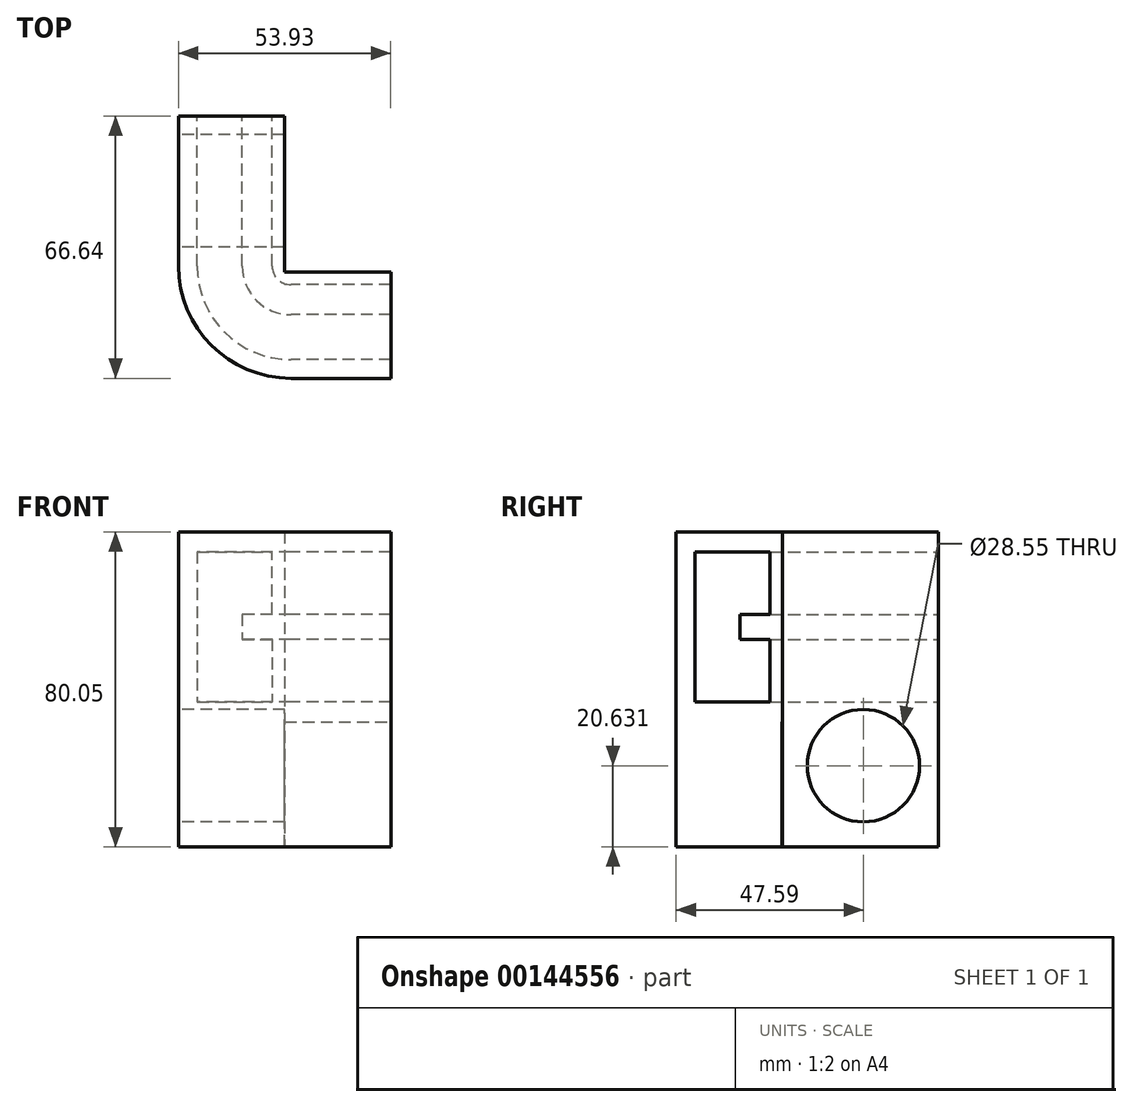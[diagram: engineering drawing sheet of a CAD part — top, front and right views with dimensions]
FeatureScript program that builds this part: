
annotation { "Feature Type Name" : "Feature", "Feature Type Description" : "" }
export const myFeature = defineFeature(function(context is Context, id is Id, definition is map)
    precondition{}
    {
        {
            var Q0;
            Q0=qCreatedBy(makeId("Front.planeOp"),FACE);
            var sketch = newSketch(context, id + "F0", { "sketchPlane" : qUnion([Q0])});
            skLineSegment(sketch, "E0.bottom", {"start": v(-12.7, 18.7) * mm, "end": v(6.35, 18.7) * mm});
            skLineSegment(sketch, "E0.top", {"start": v(-12.7, -19.4) * mm, "end": v(6.35, -19.4) * mm});
            skLineSegment(sketch, "E0.left", {"start": v(-12.7, 18.7) * mm, "end": v(-12.7, -19.4) * mm});
            skLineSegment(sketch, "E1", {"start": v(6.35, -3.53) * mm, "end": v(6.35, -19.4) * mm});
            skLineSegment(sketch, "E2", {"start": v(6.35, 2.82) * mm, "end": v(6.35, 18.7) * mm});
            skLineSegment(sketch, "E3", {"start": v(6.35, 2.82) * mm, "end": v(-1.27, 2.82) * mm});
            skLineSegment(sketch, "E4.bottom", {"start": v(-1.27, 2.82) * mm, "end": v(6.35, 2.82) * mm});
            skLineSegment(sketch, "E4.top", {"start": v(-1.27, -3.53) * mm, "end": v(6.35, -3.53) * mm});
            skLineSegment(sketch, "E4.left", {"start": v(-1.27, 2.82) * mm, "end": v(-1.27, -3.53) * mm});
            skLineSegment(sketch, "E5.bottom", {"start": v(-17.44, 23.8) * mm, "end": v(11.1, 23.8) * mm});
            skLineSegment(sketch, "E5.top", {"start": v(-17.44, -24.5) * mm, "end": v(11.1, -24.5) * mm});
            skLineSegment(sketch, "E5.left", {"start": v(-17.44, 23.8) * mm, "end": v(-17.44, -24.5) * mm});
            skLineSegment(sketch, "E5.right", {"start": v(11.1, 23.8) * mm, "end": v(11.1, -24.5) * mm});
            skLineSegment(sketch, "E6", {"start": v(-12.7, 18.7) * mm, "end": v(-17.44, 23.8) * mm, "construction": true});
            skLineSegment(sketch, "E7", {"start": v(6.35, 18.7) * mm, "end": v(11.1, 23.8) * mm, "construction": true});
            skLineSegment(sketch, "E8", {"start": v(6.35, -19.4) * mm, "end": v(11.1, -24.5) * mm, "construction": true});
            skLineSegment(sketch, "E9", {"start": v(-17.44, -24.5) * mm, "end": v(-12.7, -19.4) * mm, "construction": true});
            skSolve(sketch);
        }
        {
            var Q0;
            Q0=makeQuery(id+"F0.imprint","IMPRINT",FACE,{"disambiguationData":[TD([[makeQuery(id+"F0.imprint","IMPRINT",EDGE,{"derivedFrom":sQuery(id+"F0.wireOp",EDGE,"E0.bottom")}),1.0]])]});
            var Q1;
            Q1=sQuery(id+"F0.wireOp",EDGE,"E8");
            var Q2;
            Q2=sQuery(id+"F0.wireOp",EDGE,"E9");
            var Q3;
            Q3=sQuery(id+"F0.wireOp",EDGE,"E6");
            var Q4;
            Q4=sQuery(id+"F0.wireOp",EDGE,"E7");
            extrude(context, id + "F1", {"entities" : qUnion([Q0]), "surfaceEntities" : qUnion([Q1, Q2, Q3, Q4]), "depth" : 25.4 * mm});
        }
        {
            var Q0;
            Q0=makeQuery(id+"F1.opExtrude","CAP_FACE",FACE,{"disambiguationData":[OSD([sQuery(id+"F0.wireOp",EDGE,"E0.bottom"),sQuery(id+"F0.wireOp",EDGE,"E0.top"),sQuery(id+"F0.wireOp",EDGE,"E0.left"),sQuery(id+"F0.wireOp",EDGE,"E1"),sQuery(id+"F0.wireOp",EDGE,"E2"),sQuery(id+"F0.wireOp",EDGE,"E4.bottom"),sQuery(id+"F0.wireOp",EDGE,"E4.top"),sQuery(id+"F0.wireOp",EDGE,"E4.left"),sQuery(id+"F0.wireOp",EDGE,"E5.bottom"),sQuery(id+"F0.wireOp",EDGE,"E5.top"),sQuery(id+"F0.wireOp",EDGE,"E5.left"),sQuery(id+"F0.wireOp",EDGE,"E5.right")])],"isStart":false});
            var Q1;
            Q1=makeQuery(id+"F1.opExtrude","CAP_EDGE",EDGE,{"disambiguationData":[OSD([sQuery(id+"F0.wireOp",EDGE,"E5.right")])],"isStart":false});
            revolve(context, id + "F2", {"operationType" : NewBodyOperationType.ADD, "entities" : qUnion([Q0]), "axis" : qUnion([Q1]), "revolveType" : RevolveType.ONE_DIRECTION, "oppositeDirection" : true, "angle" : 90 * degree});
        }
        {
            var Q0;
            {var subQ0=sQuery(id+"F0.wireOp",EDGE,"E5.right");Q0=makeQuery(id+"F2.boolean.opBoolean","MERGE",FACE,{"derivedFrom":[makeQuery(id+"F1.opExtrude","SWEPT_FACE",FACE,{"disambiguationData":[OSD([subQ0])]}),makeQuery(id+"F2.opRevolve","CAP_FACE",FACE,{"disambiguationData":[OSD([sQuery(id+"F0.wireOp",EDGE,"E0.bottom"),sQuery(id+"F0.wireOp",EDGE,"E0.top"),sQuery(id+"F0.wireOp",EDGE,"E0.left"),sQuery(id+"F0.wireOp",EDGE,"E1"),sQuery(id+"F0.wireOp",EDGE,"E2"),sQuery(id+"F0.wireOp",EDGE,"E4.bottom"),sQuery(id+"F0.wireOp",EDGE,"E4.top"),sQuery(id+"F0.wireOp",EDGE,"E4.left"),sQuery(id+"F0.wireOp",EDGE,"E5.bottom"),sQuery(id+"F0.wireOp",EDGE,"E5.top"),sQuery(id+"F0.wireOp",EDGE,"E5.left"),subQ0])],"isStart":false})]});}
            extrude(context, id + "F3", {"entities" : qUnion([Q0]), "operationType" : NewBodyOperationType.ADD, "depth" : 25.4 * mm});
        }
        {
            var Q0;
            {var subQ0=sQuery(id+"F0.wireOp",EDGE,"E5.top");Q0=makeQuery(id+"F3.boolean.opBoolean","MERGE",FACE,{"derivedFrom":[makeQuery(id+"F2.boolean.opBoolean","MERGE",FACE,{"derivedFrom":[makeQuery(id+"F1.opExtrude","SWEPT_FACE",FACE,{"disambiguationData":[OSD([subQ0])]}),makeQuery(id+"F2.opRevolve","SWEPT_FACE",FACE,{"disambiguationData":[OSD([subQ0])]})]}),makeQuery(id+"F3.opExtrude","SWEPT_FACE",FACE,{"disambiguationData":[OSD([subQ0,sQuery(id+"F0.wireOp",EDGE,"E5.right")])]})]});}
            var sketch = newSketch(context, id + "F4", { "sketchPlane" : qUnion([Q0])});
            skLineSegment(sketch, "E10.bottom", {"start": v(9.53, 0) * mm, "end": v(36.5, 0) * mm});
            skLineSegment(sketch, "E10.top", {"start": v(9.53, 26.97) * mm, "end": v(36.5, 26.97) * mm});
            skLineSegment(sketch, "E10.left", {"start": v(9.53, 0) * mm, "end": v(9.53, 26.97) * mm});
            skLineSegment(sketch, "E10.right", {"start": v(36.5, 0) * mm, "end": v(36.5, 26.97) * mm});
            skSolve(sketch);
        }
        {
            var Q0;
            Q0=qSketchRegion(id+"F4",true);
            extrude(context, id + "F5", {"entities" : qUnion([Q0]), "operationType" : NewBodyOperationType.REMOVE, "endBound" : BoundingType.SYMMETRIC, "oppositeDirection" : true, "depth" : 100.3 * mm});
        }
        {
            var Q0;
            {var subQ0=sQuery(id+"F0.wireOp",EDGE,"E5.top");Q0=makeQuery(id+"F3.boolean.opBoolean","MERGE",FACE,{"derivedFrom":[makeQuery(id+"F2.boolean.opBoolean","MERGE",FACE,{"derivedFrom":[makeQuery(id+"F1.opExtrude","SWEPT_FACE",FACE,{"disambiguationData":[OSD([subQ0])]}),makeQuery(id+"F2.opRevolve","SWEPT_FACE",FACE,{"disambiguationData":[OSD([subQ0])]})]}),makeQuery(id+"F3.opExtrude","SWEPT_FACE",FACE,{"disambiguationData":[OSD([subQ0,sQuery(id+"F0.wireOp",EDGE,"E5.right")])]})]});}
            var sketch = newSketch(context, id + "F6", { "sketchPlane" : qUnion([Q0])});
            skLineSegment(sketch, "E11.bottom", {"start": v(9.53, 26.97) * mm, "end": v(36.5, 27) * mm});
            skLineSegment(sketch, "E11.top", {"start": v(9.52, 33.32) * mm, "end": v(36.5, 33.34) * mm});
            skLineSegment(sketch, "E11.left", {"start": v(9.53, 26.97) * mm, "end": v(9.52, 33.32) * mm});
            skLineSegment(sketch, "E11.right", {"start": v(36.5, 27) * mm, "end": v(36.5, 33.34) * mm});
            skPoint(sketch, "E12.oppositeSnap0", {"position": v(9.52, 30.14) * mm});
            skLineSegment(sketch, "E12.bottom", {"start": v(36.5, 53.94) * mm, "end": v(9.52, 53.94) * mm});
            skLineSegment(sketch, "E12.top", {"start": v(36.5, 47.59) * mm, "end": v(9.52, 47.59) * mm});
            skLineSegment(sketch, "E12.left", {"start": v(36.5, 53.94) * mm, "end": v(36.5, 47.59) * mm});
            skLineSegment(sketch, "E12.right", {"start": v(9.52, 53.94) * mm, "end": v(9.52, 47.59) * mm});
            skSolve(sketch);
        }
        {
            var Q0;
            Q0=makeQuery(id+"FhwqGCXb5mRywJj_1.boolean.opBoolean","MERGE",FACE,{"derivedFrom":[makeQuery(id+"F3.opExtrude","SWEPT_FACE",FACE,{"disambiguationData":[OSD([sQuery(id+"F0.wireOp",EDGE,"E5.left")])]}),makeQuery(id+"FhwqGCXb5mRywJj_1.opExtrude","SWEPT_FACE",FACE,{"disambiguationData":[OSD([sQuery(id+"F6.wireOp",EDGE,"E12.bottom")])]})]});
            var sketch = newSketch(context, id + "F7", { "sketchPlane" : qUnion([Q0])});
            skCircle(sketch, "E13", {"center": v(23.8, -35.93) * mm, "radius": 2.58 * mm});
            skLineSegment(sketch, "E14", {"start": v(23.8, -35.93) * mm, "end": v(36.5, -35.93) * mm});
            skLineSegment(sketch, "E15", {"start": v(23.8, -35.93) * mm, "end": v(11.1, -35.93) * mm});
            skSolve(sketch);
        }
        {
            var Q0;
            {var subQ0=sQuery(id+"F0.wireOp",EDGE,"E5.right");var subQ1=sQuery(id+"F0.wireOp",EDGE,"E5.left");var subQ2=sQuery(id+"F0.wireOp",EDGE,"E5.top");var subQ3=sQuery(id+"F0.wireOp",EDGE,"E5.bottom");var subQ4=sQuery(id+"F0.wireOp",EDGE,"E4.left");var subQ5=sQuery(id+"F0.wireOp",EDGE,"E4.top");var subQ6=sQuery(id+"F0.wireOp",EDGE,"E4.bottom");var subQ7=sQuery(id+"F0.wireOp",EDGE,"E2");var subQ8=sQuery(id+"F0.wireOp",EDGE,"E1");var subQ9=sQuery(id+"F0.wireOp",EDGE,"E0.left");var subQ10=sQuery(id+"F0.wireOp",EDGE,"E0.top");var subQ11=sQuery(id+"F0.wireOp",EDGE,"E0.bottom");var subQ12=makeQuery(id+"F1.opExtrude","SWEPT_FACE",FACE,{"disambiguationData":[OSD([subQ2])]});var subQ13=makeQuery(id+"F2.opRevolve","SWEPT_FACE",FACE,{"disambiguationData":[OSD([subQ2])]});var subQ14=makeQuery(id+"F3.opExtrude","SWEPT_FACE",FACE,{"disambiguationData":[OSD([subQ2,subQ0])]});Q0=makeQuery(id+"FhwqGCXb5mRywJj_1.boolean.opBoolean","SPLIT",FACE,{"disambiguationData":[TD([makeQuery(id+"F1.opExtrude","CAP_FACE",FACE,{"disambiguationData":[OSD([subQ11,subQ10,subQ9,subQ8,subQ7,subQ6,subQ5,subQ4,subQ3,subQ2,subQ1,subQ0])],"isStart":true}),subQ12,makeQuery(id+"F1.opExtrude","SWEPT_FACE",FACE,{"disambiguationData":[OSD([subQ1])]}),subQ13,makeQuery(id+"F2.opRevolve","SWEPT_FACE",FACE,{"disambiguationData":[OSD([subQ1])]}),makeQuery(id+"F3.opExtrude","SWEPT_FACE",FACE,{"disambiguationData":[OSD([subQ0])]}),subQ14,makeQuery(id+"F3.opExtrude","CAP_FACE",FACE,{"disambiguationData":[OSD([subQ11,subQ10,subQ9,subQ8,subQ7,subQ6,subQ5,subQ4,subQ3,subQ2,subQ1,subQ0])],"isStart":false}),makeQuery(id+"F5.boolean.opBoolean","COPY",FACE,{"derivedFrom":makeQuery(id+"F5.opExtrude","SWEPT_FACE",FACE,{"disambiguationData":[OSD([sQuery(id+"F4.wireOp",EDGE,"E10.top")])]})}),makeQuery(id+"F5.boolean.opBoolean","COPY",FACE,{"derivedFrom":makeQuery(id+"F5.opExtrude","SWEPT_FACE",FACE,{"disambiguationData":[OSD([sQuery(id+"F4.wireOp",EDGE,"E10.left")])]})}),makeQuery(id+"FhwqGCXb5mRywJj_1.opExtrude","SWEPT_FACE",FACE,{"disambiguationData":[OSD([sQuery(id+"F6.wireOp",EDGE,"E11.bottom")])]}),makeQuery(id+"FhwqGCXb5mRywJj_1.opExtrude","SWEPT_FACE",FACE,{"disambiguationData":[OSD([sQuery(id+"F6.wireOp",EDGE,"E11.top")])]}),makeQuery(id+"FhwqGCXb5mRywJj_1.opExtrude","SWEPT_FACE",FACE,{"disambiguationData":[OSD([sQuery(id+"F6.wireOp",EDGE,"E11.left")])]}),makeQuery(id+"FhwqGCXb5mRywJj_1.opExtrude","SWEPT_FACE",FACE,{"disambiguationData":[OSD([sQuery(id+"F6.wireOp",EDGE,"E12.top")])]}),makeQuery(id+"FhwqGCXb5mRywJj_1.opExtrude","SWEPT_FACE",FACE,{"disambiguationData":[OSD([sQuery(id+"F6.wireOp",EDGE,"E12.left")])]}),makeQuery(id+"FhwqGCXb5mRywJj_1.opExtrude","SWEPT_FACE",FACE,{"disambiguationData":[OSD([sQuery(id+"F6.wireOp",EDGE,"E12.right")])]}),makeQuery(id+"FhwqGCXb5mRywJj_1.opExtrude","SWEPT_FACE",FACE,{"disambiguationData":[OSD([subQ2,subQ1])]}),makeQuery(id+"FhwqGCXb5mRywJj_1.opExtrude","SWEPT_FACE",FACE,{"disambiguationData":[OSD([subQ2,subQ0])]})])],"derivedFrom":makeQuery(id+"F3.boolean.opBoolean","MERGE",FACE,{"derivedFrom":[makeQuery(id+"F2.boolean.opBoolean","MERGE",FACE,{"derivedFrom":[subQ12,subQ13]}),subQ14]})});}
            var sketch = newSketch(context, id + "F8", { "sketchPlane" : qUnion([Q0])});
            skLineSegment(sketch, "E16", {"start": v(-17.44, 0) * mm, "end": v(-17.44, 25.4) * mm});
            skLineSegment(sketch, "E17", {"start": v(-17.44, 25.4) * mm, "end": v(-11.1, 25.4) * mm});
            skLineSegment(sketch, "E18", {"start": v(-11.1, 25.4) * mm, "end": v(-11.1, 0) * mm});
            skLineSegment(sketch, "E19", {"start": v(-11.1, 0) * mm, "end": v(-17.44, 0) * mm});
            skLineSegment(sketch, "E20", {"start": v(9.53, 0) * mm, "end": v(3.18, 0) * mm});
            skLineSegment(sketch, "E21", {"start": v(3.18, 0) * mm, "end": v(3.18, 25.4) * mm});
            skLineSegment(sketch, "E22", {"start": v(3.18, 25.4) * mm, "end": v(9.53, 25.4) * mm});
            skLineSegment(sketch, "E23", {"start": v(9.53, 25.4) * mm, "end": v(9.53, 0) * mm});
            skSolve(sketch);
        }
        {
            var Q0;
            Q0 = qSketchRegion(id + "F8", true);
            var Q1;
            {var subQ7=sQuery(id+"F6.wireOp",EDGE,"E11.top");Q1=makeQuery(id+"F6.imprint","IMPRINT",FACE,{"disambiguationData":[TD([[makeQuery(id+"F6.imprint","IMPRINT",EDGE,{"derivedFrom":subQ7}),1.0]])]});}
            var Q2;
            {var subQ1=sQuery(id+"F6.wireOp",EDGE,"E12.top");Q2=makeQuery(id+"F6.imprint","IMPRINT",FACE,{"disambiguationData":[TD([[makeQuery(id+"F6.imprint","IMPRINT",EDGE,{"derivedFrom":subQ1}),-1.0]])]});}
            var Q3;
            {var subQ7=sQuery(id+"F6.wireOp",EDGE,"E11.top");Q3=makeQuery(id+"F6.imprint","IMPRINT",FACE,{"disambiguationData":[TD([[makeQuery(id+"F6.imprint","IMPRINT",EDGE,{"derivedFrom":subQ7}),-1.0]])]});}
            extrude(context, id + "F9", {"entities" : qUnion([Q0, Q1, Q2, Q3]), "operationType" : NewBodyOperationType.ADD, "depth" : 25.4 * mm});
        }
        {
            var Q0;
            Q0=makeQuery(id+"F9.boolean.opBoolean","MERGE",FACE,{"derivedFrom":[makeQuery(id+"F1.opExtrude","SWEPT_FACE",FACE,{"disambiguationData":[OSD([sQuery(id+"F0.wireOp",EDGE,"E5.left")])]}),makeQuery(id+"F9.opExtrude","SWEPT_FACE",FACE,{"disambiguationData":[OSD([sQuery(id+"F8.wireOp",EDGE,"E16")])]})]});
            var sketch = newSketch(context, id + "F10", { "sketchPlane" : qUnion([Q0])});
            skLineSegment(sketch, "E24", {"start": v(12.7, 23.8) * mm, "end": v(12.7, -35.92) * mm, "construction": true});
            skCircle(sketch, "E25", {"center": v(12.7, -35.92) * mm, "radius": 2.58 * mm});
            skSolve(sketch);
        }
        {
            var Q0;
            Q0 = qSketchRegion(id + "F10", true);
            extrude(context, id + "F11", {"entities" : qUnion([Q0]), "operationType" : NewBodyOperationType.REMOVE, "oppositeDirection" : true, "depth" : 50.8 * mm});
        }
        {
            var Q0;
            {var subQ0=sQuery(id+"F0.wireOp",EDGE,"E5.right");Q0=makeQuery(id+"F9.boolean.opBoolean","MERGE",FACE,{"derivedFrom":[makeQuery(id+"F3.boolean.opBoolean","MERGE",FACE,{"derivedFrom":[makeQuery(id+"F1.opExtrude","CAP_FACE",FACE,{"disambiguationData":[OSD([sQuery(id+"F0.wireOp",EDGE,"E0.bottom"),sQuery(id+"F0.wireOp",EDGE,"E0.top"),sQuery(id+"F0.wireOp",EDGE,"E0.left"),sQuery(id+"F0.wireOp",EDGE,"E1"),sQuery(id+"F0.wireOp",EDGE,"E2"),sQuery(id+"F0.wireOp",EDGE,"E4.bottom"),sQuery(id+"F0.wireOp",EDGE,"E4.top"),sQuery(id+"F0.wireOp",EDGE,"E4.left"),sQuery(id+"F0.wireOp",EDGE,"E5.bottom"),sQuery(id+"F0.wireOp",EDGE,"E5.top"),sQuery(id+"F0.wireOp",EDGE,"E5.left"),subQ0])],"isStart":true}),makeQuery(id+"F3.opExtrude","SWEPT_FACE",FACE,{"disambiguationData":[OSD([subQ0])]})]}),makeQuery(id+"F9.opExtrude","SWEPT_FACE",FACE,{"disambiguationData":[OSD([sQuery(id+"F8.wireOp",EDGE,"E19")])]}),makeQuery(id+"F9.opExtrude","SWEPT_FACE",FACE,{"disambiguationData":[OSD([sQuery(id+"F8.wireOp",EDGE,"E20")])]})]});}
            var sketch = newSketch(context, id + "F12", { "sketchPlane" : qUnion([Q0])});
            skLineSegment(sketch, "E26", {"start": v(1.27, -0.35) * mm, "end": v(-9.53, -0.35) * mm});
            skSolve(sketch);
        }
        {
            var Q0;
            Q0=makeQuery(id+"F12.imprint","IMPRINT",FACE,{"disambiguationData":[TD([[makeQuery(id+"F12.imprint","IMPRINT",EDGE,{"derivedFrom":makeQuery(id+"F1.opExtrude","CAP_EDGE",EDGE,{"disambiguationData":[OSD([sQuery(id+"F0.wireOp",EDGE,"E0.bottom")])],"isStart":true})}),-1.0]])]});
            extrude(context, id + "F13", {"entities" : qUnion([Q0]), "operationType" : NewBodyOperationType.ADD, "depth" : 12.7 * mm, "offsetDistance" : 25.4 * mm});
        }
        {
            var Q0;
            {var subQ0=sQuery(id+"F0.wireOp",EDGE,"E5.left");var subQ1=sQuery(id+"F0.wireOp",EDGE,"E5.top");Q0=makeQuery(id+"F13.boolean.opBoolean","MERGE",FACE,{"derivedFrom":[makeQuery(id+"F9.boolean.opBoolean","MERGE",FACE,{"derivedFrom":[makeQuery(id+"F1.opExtrude","SWEPT_FACE",FACE,{"disambiguationData":[OSD([subQ0])]}),makeQuery(id+"F9.opExtrude","SWEPT_FACE",FACE,{"disambiguationData":[OSD([subQ1,subQ0]),TDD([makeQuery(id+"F6.imprint","IMPRINT",EDGE,{"derivedFrom":makeQuery(id+"F1.opExtrude","SWEPT_EDGE",EDGE,{"disambiguationData":[OSD([subQ1,subQ0])]})})])]})]}),makeQuery(id+"F13.opExtrude","SWEPT_FACE",FACE,{"disambiguationData":[OSD([subQ1,subQ0,sQuery(id+"F0.wireOp",EDGE,"E5.right")])]})]});}
            var sketch = newSketch(context, id + "F14", { "sketchPlane" : qUnion([Q0])});
            skLineSegment(sketch, "E27", {"start": v(12.7, -35.92) * mm, "end": v(12.7, -49.9) * mm});
            skLineSegment(sketch, "E28", {"start": v(-12.7, -35.62) * mm, "end": v(25.4, -35.62) * mm});
            skCircle(sketch, "E29", {"center": v(6.35, -35.62) * mm, "radius": 14.27 * mm});
            skSolve(sketch);
        }
        {
            var Q0;
            {var subQ0=sQuery(id+"F0.wireOp",EDGE,"E5.right");var subQ1=sQuery(id+"F0.wireOp",EDGE,"E5.top");Q0=makeQuery(id+"F13.boolean.opBoolean","MERGE",FACE,{"derivedFrom":[makeQuery(id+"F9.opExtrude","CAP_FACE",FACE,{"disambiguationData":[OSD([subQ1,sQuery(id+"F0.wireOp",EDGE,"E5.left"),subQ0,sQuery(id+"F4.wireOp",EDGE,"E10.left"),sQuery(id+"F6.wireOp",EDGE,"E11.bottom"),sQuery(id+"F6.wireOp",EDGE,"E12.bottom"),sQuery(id+"F6.wireOp",EDGE,"E12.left")])],"isStart":false}),makeQuery(id+"F13.opExtrude","SWEPT_FACE",FACE,{"disambiguationData":[OSD([subQ1,subQ0])]})]});}
            extrude(context, id + "F15", {"entities" : qUnion([Q0]), "operationType" : NewBodyOperationType.ADD, "depth" : 6.35 * mm, "offsetDistance" : 25.4 * mm});
        }
        {
            var Q0;
            {var subQ0=sQuery(id+"F14.wireOp",EDGE,"E29");var subQ1=sQuery(id+"F14.wireOp",EDGE,"E28");var subQ2=makeQuery(id+"F14.imprint","INTERSECT",VERTEX,{"disambiguationData":[OD(0.0)],"derivedFrom":[subQ1,subQ0]});Q0=makeQuery(id+"F14.imprint","IMPRINT",FACE,{"disambiguationData":[TD([[makeQuery(id+"F14.imprint","IMPRINT",EDGE,{"disambiguationData":[TD([[subQ2,-1.0]])],"derivedFrom":subQ1}),1.0]])]});}
            var Q1;
            {var subQ0=sQuery(id+"F14.wireOp",EDGE,"E29");var subQ1=sQuery(id+"F14.wireOp",EDGE,"E27");var subQ2=makeQuery(id+"F14.imprint","INTERSECT",VERTEX,{"derivedFrom":[subQ1,subQ0]});Q1=makeQuery(id+"F14.imprint","IMPRINT",FACE,{"disambiguationData":[TD([[makeQuery(id+"F14.imprint","IMPRINT",EDGE,{"disambiguationData":[TD([[subQ2,1.0]])],"derivedFrom":subQ1}),-1.0]])]});}
            var Q2;
            {var subQ0=sQuery(id+"F14.wireOp",EDGE,"E29");var subQ1=sQuery(id+"F14.wireOp",EDGE,"E27");var subQ2=makeQuery(id+"F14.imprint","INTERSECT",VERTEX,{"derivedFrom":[subQ1,subQ0]});Q2=makeQuery(id+"F14.imprint","IMPRINT",FACE,{"disambiguationData":[TD([[makeQuery(id+"F14.imprint","IMPRINT",EDGE,{"disambiguationData":[TD([[subQ2,1.0]])],"derivedFrom":subQ1}),1.0]])]});}
            extrude(context, id + "F16", {"entities" : qUnion([Q0, Q1, Q2]), "operationType" : NewBodyOperationType.REMOVE, "oppositeDirection" : true, "depth" : 50.8 * mm, "offsetDistance" : 25.4 * mm});
        }
    });
